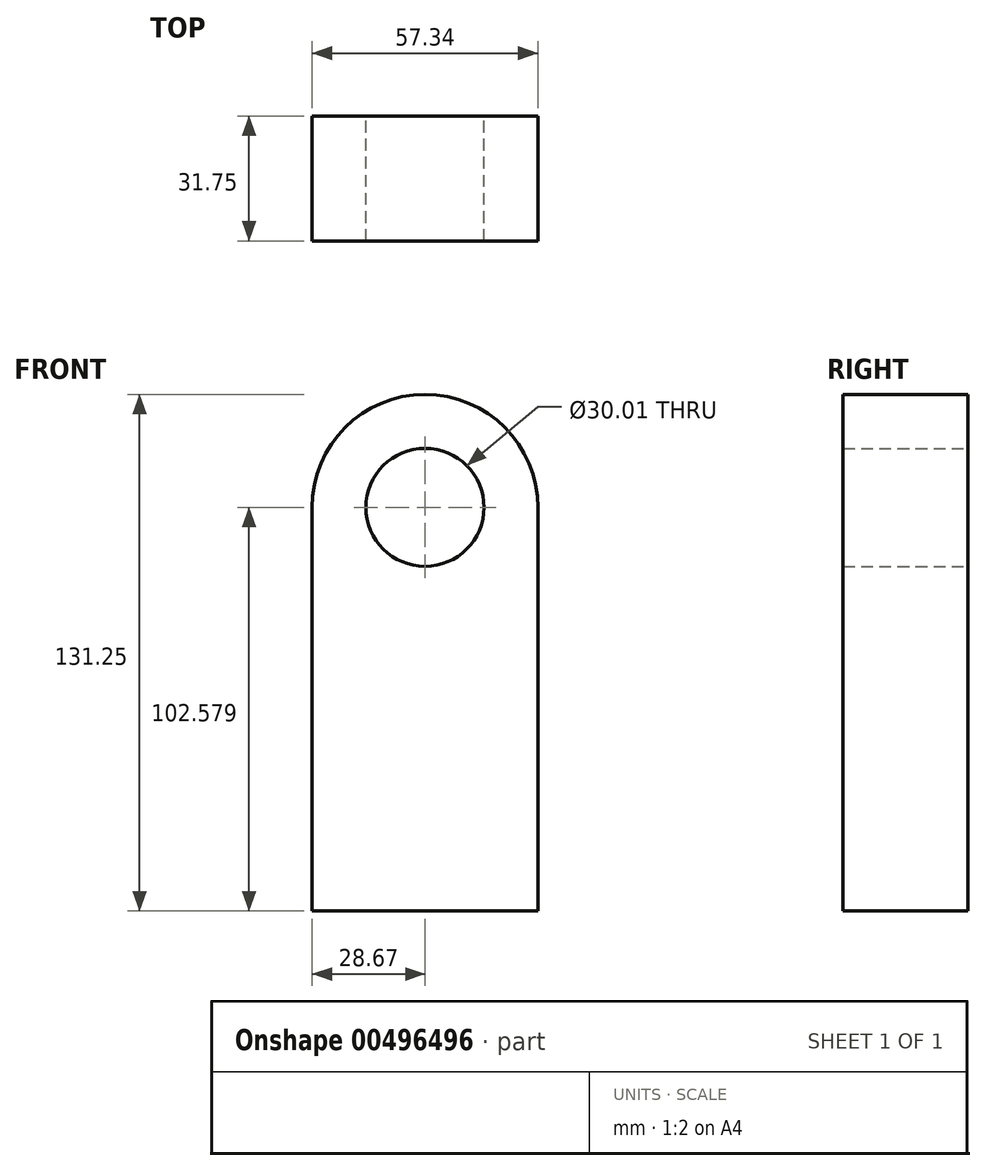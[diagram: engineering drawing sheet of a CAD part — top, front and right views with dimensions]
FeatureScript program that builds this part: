
annotation { "Feature Type Name" : "Feature", "Feature Type Description" : "" }
export const myFeature = defineFeature(function(context is Context, id is Id, definition is map)
    precondition{}
    {
        {
            var Q0;
            Q0=qCreatedBy(makeId("Front.planeOp"),FACE);
            var sketch = newSketch(context, id + "F0", { "sketchPlane" : qUnion([Q0])});
            skLineSegment(sketch, "E0.top", {"start": v(28.67, -51.29) * mm, "end": v(-28.67, -51.29) * mm});
            skLineSegment(sketch, "E0.left", {"start": v(28.67, 51.29) * mm, "end": v(28.67, -51.29) * mm});
            skLineSegment(sketch, "E0.right", {"start": v(-28.67, 51.29) * mm, "end": v(-28.67, -51.29) * mm});
            skPoint(sketch, "E0.middle", {"position": v(0, 0) * mm});
            skArc(sketch, "E1", {"start": v(28.67, 51.29) * mm, "mid": v(0, 79.96) * mm, "end": v(-28.67, 51.29) * mm});
            skCircle(sketch, "E2", {"center": v(0, 51.29) * mm, "radius": 15 * mm});
            skSolve(sketch);
        }
        {
            var Q0;
            Q0=makeQuery(id+"F0.imprint","IMPRINT",FACE,{"disambiguationData":[TD([[makeQuery(id+"F0.imprint","IMPRINT",EDGE,{"derivedFrom":sQuery(id+"F0.wireOp",EDGE,"E0.top")}),-1.0]])]});
            extrude(context, id + "F1", {"entities" : qUnion([Q0]), "depth" : 31.75 * mm});
        }
    });
